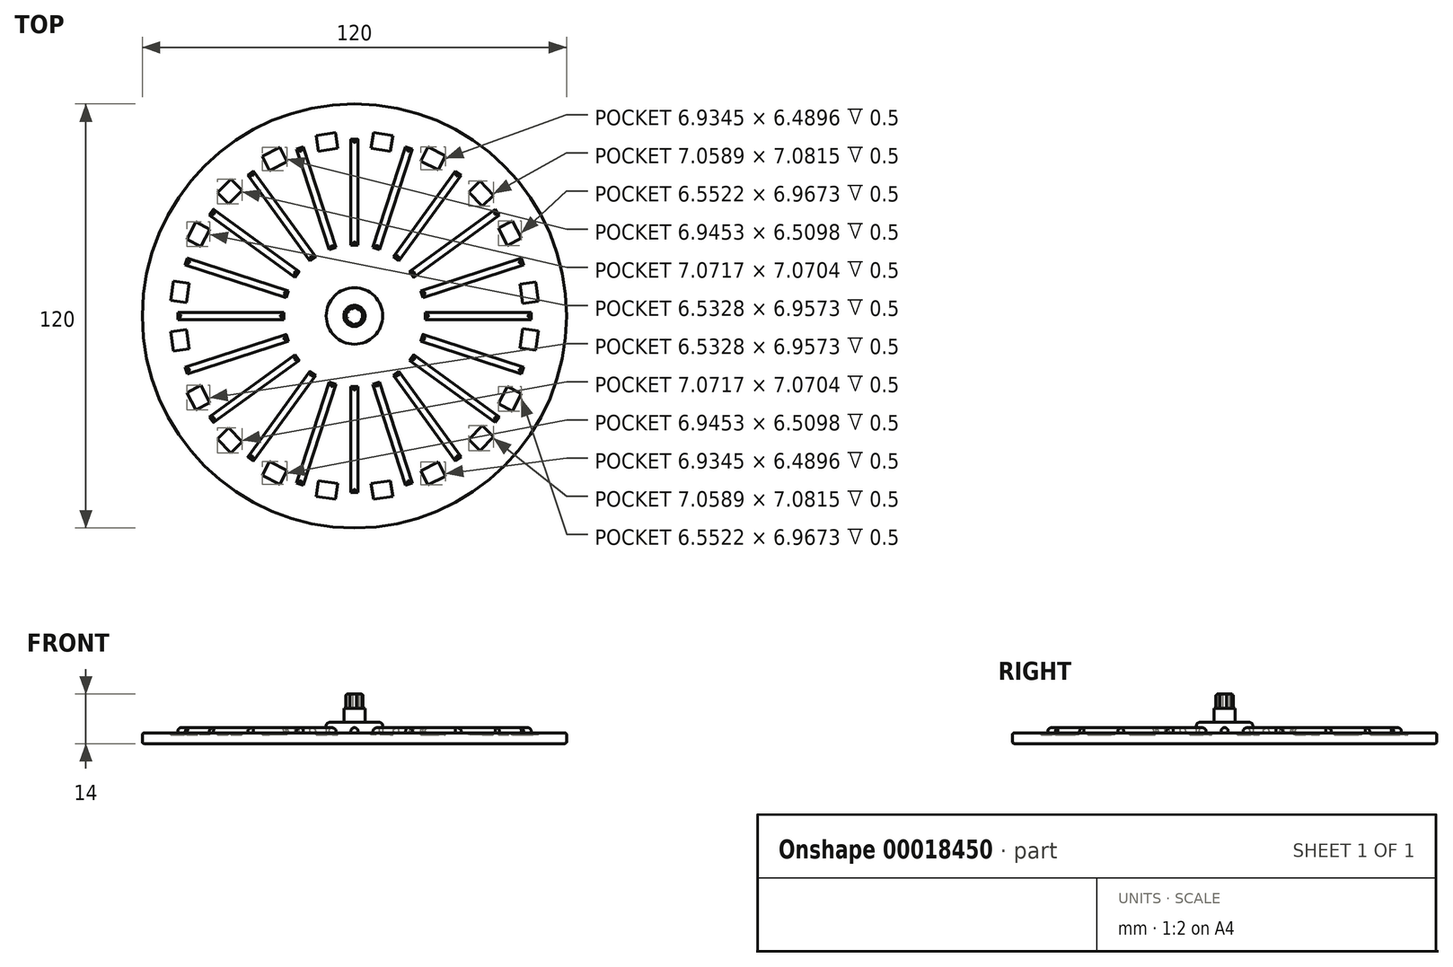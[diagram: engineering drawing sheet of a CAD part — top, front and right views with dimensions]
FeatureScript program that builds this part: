
annotation { "Feature Type Name" : "Feature", "Feature Type Description" : "" }
export const myFeature = defineFeature(function(context is Context, id is Id, definition is map)
    precondition{}
    {
        {
            var Q0;
            Q0=qCreatedBy(makeId("Top.planeOp"),FACE);
            var sketch = newSketch(context, id + "F0", { "sketchPlane" : qUnion([Q0])});
            skCircle(sketch, "E0", {"center": v(0, 0) * mm, "radius": 60 * mm});
            skSolve(sketch);
        }
        {
            var Q0;
            Q0=makeQuery(id+"F0.imprint","IMPRINT",FACE,{"disambiguationData":[TD([[makeQuery(id+"F0.imprint","IMPRINT",EDGE,{"derivedFrom":sQuery(id+"F0.wireOp",EDGE,"E0")}),1.0]])]});
            extrude(context, id + "F1", {"entities" : qUnion([Q0]), "depth" : 3 * mm});
        }
        {
            var Q0;
            Q0=makeQuery(id+"F1.opExtrude","CAP_EDGE",EDGE,{"disambiguationData":[OSD([sQuery(id+"F0.wireOp",EDGE,"E0")])],"isStart":false});
            var Q1;
            Q1=makeQuery(id+"F1.opExtrude","CAP_EDGE",EDGE,{"disambiguationData":[OSD([sQuery(id+"F0.wireOp",EDGE,"E0")])],"isStart":true});
            fillet(context, id + "F2", {"entities" : qUnion([Q0, Q1]), "radius" : 0.5 * mm, "tangentPropagation" : true, "allowEdgeOverflow" : false});
        }
        {
            var Q0;
            Q0=makeQuery(id+"F1.opExtrude","CAP_FACE",FACE,{"disambiguationData":[OSD([sQuery(id+"F0.wireOp",EDGE,"E0")])],"isStart":false});
            var sketch = newSketch(context, id + "F3", { "sketchPlane" : qUnion([Q0])});
            skLineSegment(sketch, "E1", {"start": v(0, 0) * mm, "end": v(0, 59.5) * mm, "construction": true});
            skCircle(sketch, "E2", {"center": v(0, 0) * mm, "radius": 20 * mm, "construction": true});
            skCircle(sketch, "E3", {"center": v(0, 0) * mm, "radius": 50 * mm, "construction": true});
            skCircle(sketch, "E4", {"center": v(0, 0) * mm, "radius": 35 * mm, "construction": true});
            skLineSegment(sketch, "E5.rect.bottom", {"start": v(1, 49.99) * mm, "end": v(-1, 49.99) * mm});
            skLineSegment(sketch, "E5.rect.top", {"start": v(1, 20.01) * mm, "end": v(-1, 20.01) * mm});
            skLineSegment(sketch, "E5.rect.left", {"start": v(1, 49.99) * mm, "end": v(1, 20.01) * mm});
            skLineSegment(sketch, "E5.rect.right", {"start": v(-1, 49.99) * mm, "end": v(-1, 20.01) * mm});
            skPoint(sketch, "E5.rect.middle", {"position": v(0, 35) * mm});
            skCircle(sketch, "E6", {"center": v(0, 0) * mm, "radius": 8 * mm});
            skCircle(sketch, "E7", {"center": v(0, 0) * mm, "radius": 45 * mm, "construction": true});
            skSolve(sketch);
        }
        {
            var Q0;
            Q0=makeQuery(id+"F3.imprint","IMPRINT",FACE,{"disambiguationData":[TD([[makeQuery(id+"F3.imprint","IMPRINT",EDGE,{"derivedFrom":sQuery(id+"F3.wireOp",EDGE,"E5.rect.bottom")}),1.0]])]});
            extrude(context, id + "F4", {"entities" : qUnion([Q0]), "depth" : 1.5 * mm});
        }
        {
            var Q0;
            Q0=makeQuery(id+"F4.opExtrude","CAP_EDGE",EDGE,{"disambiguationData":[OSD([sQuery(id+"F3.wireOp",EDGE,"E5.rect.left")])],"isStart":false});
            var Q1;
            Q1=makeQuery(id+"F4.opExtrude","CAP_EDGE",EDGE,{"disambiguationData":[OSD([sQuery(id+"F3.wireOp",EDGE,"E5.rect.right")])],"isStart":false});
            var Q2;
            Q2=makeQuery(id+"F4.opExtrude","CAP_EDGE",EDGE,{"disambiguationData":[OSD([sQuery(id+"F3.wireOp",EDGE,"E5.rect.top")])],"isStart":false});
            var Q3;
            Q3=makeQuery(id+"F4.opExtrude","CAP_EDGE",EDGE,{"disambiguationData":[OSD([sQuery(id+"F3.wireOp",EDGE,"E5.rect.bottom")])],"isStart":false});
            fillet(context, id + "F5", {"entities" : qUnion([Q0, Q1, Q2, Q3]), "radius" : 1 * mm, "tangentPropagation" : true, "allowEdgeOverflow" : false});
        }
        {
            var Q0;
            Q0=makeQuery(id+"F4.opExtrude","SWEPT_BODY",BODY,{"disambiguationData":[OSD([sQuery(id+"F3.wireOp",EDGE,"E5.rect.bottom"),sQuery(id+"F3.wireOp",EDGE,"E5.rect.top"),sQuery(id+"F3.wireOp",EDGE,"E5.rect.left"),sQuery(id+"F3.wireOp",EDGE,"E5.rect.right")])]});
            var Q1;
            {var subQ0=sQuery(id+"F0.wireOp",EDGE,"E0");Q1=makeQuery(id+"F2.opFillet","BLEND_EDGE",EDGE,{"blendedFrom":[makeQuery(id+"F1.opExtrude","CAP_EDGE",EDGE,{"disambiguationData":[OSD([subQ0])],"isStart":false}),makeQuery(id+"F1.opExtrude","SWEPT_FACE",FACE,{"disambiguationData":[OSD([subQ0])]})],"blendedInto":[makeQuery(id+"F1.opExtrude","SWEPT_FACE",FACE,{"disambiguationData":[OSD([subQ0])]})]});}
            circularPattern(context, id + "F6", {"operationType" : NewBodyOperationType.ADD, "entities" : qUnion([Q0]), "axis" : qUnion([Q1]), "angle" : 18 * degree, "instanceCount" : round(23)});
        }
        {
            var Q0;
            Q0=makeQuery(id+"F3.imprint","IMPRINT",FACE,{"disambiguationData":[TD([[makeQuery(id+"F3.imprint","IMPRINT",EDGE,{"derivedFrom":sQuery(id+"F3.wireOp",EDGE,"E6")}),1.0]])]});
            extrude(context, id + "F7", {"entities" : qUnion([Q0]), "operationType" : NewBodyOperationType.ADD, "depth" : 3 * mm});
        }
        {
            var Q0;
            Q0=makeQuery(id+"F7.opExtrude","CAP_EDGE",EDGE,{"disambiguationData":[OSD([sQuery(id+"F3.wireOp",EDGE,"E6")])],"isStart":false});
            fillet(context, id + "F8", {"entities" : qUnion([Q0]), "radius" : 1 * mm, "tangentPropagation" : true, "allowEdgeOverflow" : false});
        }
        {
            var Q0;
            Q0=makeQuery(id+"F7.opExtrude","CAP_FACE",FACE,{"disambiguationData":[OSD([sQuery(id+"F3.wireOp",EDGE,"E6")])],"isStart":false});
            var sketch = newSketch(context, id + "F9", { "sketchPlane" : qUnion([Q0])});
            skCircle(sketch, "E8", {"center": v(0, 0) * mm, "radius": 3 * mm});
            skSolve(sketch);
        }
        {
            var Q0;
            Q0=makeQuery(id+"F9.imprint","IMPRINT",FACE,{"disambiguationData":[TD([[makeQuery(id+"F9.imprint","IMPRINT",EDGE,{"derivedFrom":sQuery(id+"F9.wireOp",EDGE,"E8")}),1.0]])]});
            extrude(context, id + "F10", {"entities" : qUnion([Q0]), "operationType" : NewBodyOperationType.ADD, "depth" : 4 * mm});
        }
        {
            var Q0;
            Q0=makeQuery(id+"F10.opExtrude","CAP_FACE",FACE,{"disambiguationData":[OSD([sQuery(id+"F9.wireOp",EDGE,"E8")])],"isStart":false});
            var sketch = newSketch(context, id + "F11", { "sketchPlane" : qUnion([Q0])});
            skCircle(sketch, "E9.cCircle", {"center": v(0, 0) * mm, "radius": 2.5 * mm, "construction": true});
            skLineSegment(sketch, "E9.0", {"start": v(2.13, -1.3) * mm, "end": v(0.59, -2.43) * mm});
            skLineSegment(sketch, "E9.1", {"start": v(0.59, -2.43) * mm, "end": v(-1.3, -2.13) * mm});
            skLineSegment(sketch, "E9.2", {"start": v(-1.3, -2.13) * mm, "end": v(-2.43, -0.59) * mm});
            skLineSegment(sketch, "E9.3", {"start": v(-2.43, -0.59) * mm, "end": v(-2.13, 1.3) * mm});
            skLineSegment(sketch, "E9.4", {"start": v(-2.13, 1.3) * mm, "end": v(-0.59, 2.43) * mm});
            skLineSegment(sketch, "E9.5", {"start": v(-0.59, 2.43) * mm, "end": v(1.3, 2.13) * mm});
            skLineSegment(sketch, "E9.6", {"start": v(1.3, 2.13) * mm, "end": v(2.43, 0.59) * mm});
            skLineSegment(sketch, "E9.7", {"start": v(2.43, 0.59) * mm, "end": v(2.13, -1.3) * mm});
            skSolve(sketch);
        }
        {
            var Q0;
            Q0=makeQuery(id+"F11.imprint","IMPRINT",FACE,{"disambiguationData":[TD([[makeQuery(id+"F11.imprint","IMPRINT",EDGE,{"derivedFrom":sQuery(id+"F11.wireOp",EDGE,"E9.0")}),-1.0]])]});
            extrude(context, id + "F12", {"entities" : qUnion([Q0]), "operationType" : NewBodyOperationType.ADD, "depth" : 4 * mm});
        }
        {
            var Q0;
            Q0=makeQuery(id+"F12.opExtrude","CAP_EDGE",EDGE,{"disambiguationData":[OSD([sQuery(id+"F11.wireOp",EDGE,"E9.3")])],"isStart":false});
            var Q1;
            Q1=makeQuery(id+"F12.opExtrude","CAP_EDGE",EDGE,{"disambiguationData":[OSD([sQuery(id+"F11.wireOp",EDGE,"E9.2")])],"isStart":false});
            var Q2;
            Q2=makeQuery(id+"F12.opExtrude","CAP_EDGE",EDGE,{"disambiguationData":[OSD([sQuery(id+"F11.wireOp",EDGE,"E9.1")])],"isStart":false});
            var Q3;
            Q3=makeQuery(id+"F12.opExtrude","CAP_EDGE",EDGE,{"disambiguationData":[OSD([sQuery(id+"F11.wireOp",EDGE,"E9.4")])],"isStart":false});
            var Q4;
            Q4=makeQuery(id+"F12.opExtrude","CAP_EDGE",EDGE,{"disambiguationData":[OSD([sQuery(id+"F11.wireOp",EDGE,"E9.5")])],"isStart":false});
            var Q5;
            Q5=makeQuery(id+"F12.opExtrude","CAP_EDGE",EDGE,{"disambiguationData":[OSD([sQuery(id+"F11.wireOp",EDGE,"E9.6")])],"isStart":false});
            var Q6;
            Q6=makeQuery(id+"F12.opExtrude","CAP_EDGE",EDGE,{"disambiguationData":[OSD([sQuery(id+"F11.wireOp",EDGE,"E9.7")])],"isStart":false});
            var Q7;
            Q7=makeQuery(id+"F12.opExtrude","CAP_EDGE",EDGE,{"disambiguationData":[OSD([sQuery(id+"F11.wireOp",EDGE,"E9.0")])],"isStart":false});
            fillet(context, id + "F13", {"entities" : qUnion([Q0, Q1, Q2, Q3, Q4, Q5, Q6, Q7]), "radius" : 0.5 * mm, "allowEdgeOverflow" : false});
        }
        {
            var Q0;
            Q0=makeQuery(id+"F3.imprint","IMPRINT",FACE,{"disambiguationData":[TD([[makeQuery(id+"F3.imprint","IMPRINT",EDGE,{"derivedFrom":sQuery(id+"F3.wireOp",EDGE,"E5.rect.bottom")}),-1.0]])]});
            var sketch = newSketch(context, id + "F14", { "sketchPlane" : qUnion([Q0])});
            skLineSegment(sketch, "E10", {"start": v(0, 0) * mm, "end": v(9.16, 58.76) * mm, "construction": true});
            skLineSegment(sketch, "E11", {"start": v(0, 0) * mm, "end": v(18.06, 56.37) * mm, "construction": true});
            skLineSegment(sketch, "E12", {"start": v(0, 0) * mm, "end": v(0, 59.7) * mm, "construction": true});
            skLineSegment(sketch, "E13", {"start": v(0, 59.7) * mm, "end": v(9.16, 58.76) * mm, "construction": true});
            skLineSegment(sketch, "E14", {"start": v(9.16, 58.76) * mm, "end": v(0, 59.7) * mm, "construction": true});
            skLineSegment(sketch, "E15", {"start": v(9.16, 58.76) * mm, "end": v(18.06, 56.37) * mm, "construction": true});
            skLineSegment(sketch, "E16", {"start": v(7.33, 47.02) * mm, "end": v(4.7, 47.43) * mm});
            skLineSegment(sketch, "E17", {"start": v(7.33, 47.02) * mm, "end": v(10.14, 46.58) * mm});
            skLineSegment(sketch, "E18", {"start": v(10.14, 46.58) * mm, "end": v(10.83, 51.03) * mm});
            skLineSegment(sketch, "E19", {"start": v(10.83, 51.03) * mm, "end": v(5.4, 51.87) * mm});
            skLineSegment(sketch, "E20", {"start": v(5.4, 51.87) * mm, "end": v(4.7, 47.43) * mm});
            skLineSegment(sketch, "E21.0.MirrorCS", {"start": v(-10.83, 51.03) * mm, "end": v(-5.4, 51.87) * mm});
            skLineSegment(sketch, "E22.0.MirrorCS", {"start": v(-5.4, 51.87) * mm, "end": v(-4.7, 47.43) * mm});
            skLineSegment(sketch, "E23.0.MirrorCS", {"start": v(-10.14, 46.58) * mm, "end": v(-10.83, 51.03) * mm});
            skLineSegment(sketch, "E24.0.MirrorCS", {"start": v(-7.33, 47.02) * mm, "end": v(-4.7, 47.43) * mm});
            skLineSegment(sketch, "E25.0.MirrorCS", {"start": v(-7.33, 47.02) * mm, "end": v(-10.14, 46.58) * mm});
            skLineSegment(sketch, "E26.0.MirrorCS", {"start": v(21.36, 42.52) * mm, "end": v(18.81, 43.8) * mm});
            skLineSegment(sketch, "E27.0.MirrorCS", {"start": v(25.75, 45.35) * mm, "end": v(23.73, 41.33) * mm});
            skLineSegment(sketch, "E28.0.MirrorCS", {"start": v(18.81, 43.8) * mm, "end": v(20.83, 47.82) * mm});
            skLineSegment(sketch, "E29.0.MirrorCS", {"start": v(20.83, 47.82) * mm, "end": v(25.75, 45.35) * mm});
            skLineSegment(sketch, "E30.0.MirrorCS", {"start": v(21.36, 42.52) * mm, "end": v(23.73, 41.33) * mm});
            skLineSegment(sketch, "E31", {"start": v(0, 0) * mm, "end": v(-18.56, 57.25) * mm, "construction": true});
            skLineSegment(sketch, "E32", {"start": v(0, 0) * mm, "end": v(-34.89, 48) * mm, "construction": true});
            skLineSegment(sketch, "E33.0.MirrorCS", {"start": v(-19.12, 43.67) * mm, "end": v(-21.17, 47.68) * mm});
            skLineSegment(sketch, "E34.0.MirrorCS", {"start": v(-26.07, 45.17) * mm, "end": v(-24.02, 41.17) * mm});
            skLineSegment(sketch, "E35.0.MirrorCS", {"start": v(-21.17, 47.68) * mm, "end": v(-26.07, 45.17) * mm});
            skLineSegment(sketch, "E36.0.MirrorCS", {"start": v(-21.65, 42.37) * mm, "end": v(-19.12, 43.67) * mm});
            skLineSegment(sketch, "E37.0.MirrorCS", {"start": v(-21.65, 42.37) * mm, "end": v(-24.02, 41.17) * mm});
            skLineSegment(sketch, "E38.0.MirrorCS", {"start": v(-33.62, 33.68) * mm, "end": v(-31.74, 35.55) * mm});
            skLineSegment(sketch, "E39.0.MirrorCS", {"start": v(-33.62, 33.68) * mm, "end": v(-35.63, 31.67) * mm});
            skLineSegment(sketch, "E40.0.MirrorCS", {"start": v(-35.63, 31.67) * mm, "end": v(-38.81, 34.85) * mm});
            skLineSegment(sketch, "E41.0.MirrorCS", {"start": v(-38.81, 34.85) * mm, "end": v(-34.92, 38.74) * mm});
            skLineSegment(sketch, "E42.0.MirrorCS", {"start": v(-34.92, 38.74) * mm, "end": v(-31.74, 35.55) * mm});
            skLineSegment(sketch, "E43", {"start": v(0, 0) * mm, "end": v(-48.36, 35.52) * mm, "construction": true});
            skLineSegment(sketch, "E44", {"start": v(0, 0) * mm, "end": v(-58.04, 18.6) * mm, "construction": true});
            skLineSegment(sketch, "E45", {"start": v(0, 0) * mm, "end": v(61.65, 0) * mm, "construction": true});
            skLineSegment(sketch, "E46", {"start": v(61.65, 0) * mm, "end": v(-61.86, 0) * mm, "construction": true});
            skLineSegment(sketch, "E47", {"start": v(0, 0) * mm, "end": v(34.29, 46.69) * mm, "construction": true});
            skLineSegment(sketch, "E48", {"start": v(0, 0) * mm, "end": v(48.15, 35) * mm, "construction": true});
            skLineSegment(sketch, "E49", {"start": v(0, 0) * mm, "end": v(57.22, 18.4) * mm, "construction": true});
            skLineSegment(sketch, "E50.0.MirrorCS", {"start": v(-40.88, 24.52) * mm, "end": v(-44.87, 26.6) * mm});
            skLineSegment(sketch, "E51.0.MirrorCS", {"start": v(-47.41, 21.72) * mm, "end": v(-43.42, 19.64) * mm});
            skLineSegment(sketch, "E52.0.MirrorCS", {"start": v(-44.87, 26.6) * mm, "end": v(-47.41, 21.72) * mm});
            skLineSegment(sketch, "E53.0.MirrorCS", {"start": v(-42.2, 22) * mm, "end": v(-40.88, 24.52) * mm});
            skLineSegment(sketch, "E54.0.MirrorCS", {"start": v(-42.2, 22) * mm, "end": v(-43.42, 19.64) * mm});
            skLineSegment(sketch, "E55.0.MirrorCS", {"start": v(-51.2, 9.88) * mm, "end": v(-46.75, 9.25) * mm});
            skLineSegment(sketch, "E56.0.MirrorCS", {"start": v(-47.52, 3.8) * mm, "end": v(-51.97, 4.43) * mm});
            skLineSegment(sketch, "E57.0.MirrorCS", {"start": v(-51.97, 4.43) * mm, "end": v(-51.2, 9.88) * mm});
            skLineSegment(sketch, "E58.0.MirrorCS", {"start": v(-47.12, 6.62) * mm, "end": v(-47.52, 3.8) * mm});
            skLineSegment(sketch, "E59.0.MirrorCS", {"start": v(-47.12, 6.62) * mm, "end": v(-46.75, 9.25) * mm});
            skLineSegment(sketch, "E60.0.MirrorCS", {"start": v(39.4, 34.2) * mm, "end": v(35.57, 38.14) * mm});
            skLineSegment(sketch, "E61.0.MirrorCS", {"start": v(36.16, 31.06) * mm, "end": v(39.4, 34.2) * mm});
            skLineSegment(sketch, "E62.0.MirrorCS", {"start": v(35.57, 38.14) * mm, "end": v(32.33, 35.01) * mm});
            skLineSegment(sketch, "E63.0.MirrorCS", {"start": v(34.18, 33.1) * mm, "end": v(32.33, 35.01) * mm});
            skLineSegment(sketch, "E64.0.MirrorCS", {"start": v(34.18, 33.1) * mm, "end": v(36.16, 31.06) * mm});
            skLineSegment(sketch, "E65.0.MirrorCS", {"start": v(42.04, 22.3) * mm, "end": v(40.7, 24.8) * mm});
            skLineSegment(sketch, "E66.0.MirrorCS", {"start": v(47.26, 22.05) * mm, "end": v(43.29, 19.95) * mm});
            skLineSegment(sketch, "E67.0.MirrorCS", {"start": v(44.68, 26.91) * mm, "end": v(47.26, 22.05) * mm});
            skLineSegment(sketch, "E68.0.MirrorCS", {"start": v(40.7, 24.8) * mm, "end": v(44.68, 26.91) * mm});
            skLineSegment(sketch, "E69.0.MirrorCS", {"start": v(42.04, 22.3) * mm, "end": v(43.29, 19.95) * mm});
            skLineSegment(sketch, "E70.0.MirrorCS", {"start": v(47.15, 6.4) * mm, "end": v(46.8, 9.02) * mm});
            skLineSegment(sketch, "E71.0.MirrorCS", {"start": v(51.26, 9.63) * mm, "end": v(46.8, 9.02) * mm});
            skLineSegment(sketch, "E72.0.MirrorCS", {"start": v(52, 4.18) * mm, "end": v(51.26, 9.63) * mm});
            skLineSegment(sketch, "E73.0.MirrorCS", {"start": v(47.54, 3.57) * mm, "end": v(52, 4.18) * mm});
            skLineSegment(sketch, "E74.0.MirrorCS", {"start": v(47.15, 6.4) * mm, "end": v(47.54, 3.57) * mm});
            skLineSegment(sketch, "E75.0.MirrorCS", {"start": v(-47.52, -3.8) * mm, "end": v(-51.97, -4.43) * mm});
            skLineSegment(sketch, "E76.0.MirrorCS", {"start": v(-51.97, -4.43) * mm, "end": v(-51.2, -9.88) * mm});
            skLineSegment(sketch, "E77.0.MirrorCS", {"start": v(-47.12, -6.62) * mm, "end": v(-46.75, -9.25) * mm});
            skLineSegment(sketch, "E78.0.MirrorCS", {"start": v(-47.12, -6.62) * mm, "end": v(-47.52, -3.8) * mm});
            skLineSegment(sketch, "E79.0.MirrorCS", {"start": v(-51.2, -9.88) * mm, "end": v(-46.75, -9.25) * mm});
            skLineSegment(sketch, "E80.0.MirrorCS", {"start": v(-47.41, -21.72) * mm, "end": v(-43.42, -19.64) * mm});
            skLineSegment(sketch, "E81.0.MirrorCS", {"start": v(-44.87, -26.6) * mm, "end": v(-47.41, -21.72) * mm});
            skLineSegment(sketch, "E82.0.MirrorCS", {"start": v(-42.2, -22) * mm, "end": v(-43.42, -19.64) * mm});
            skLineSegment(sketch, "E83.0.MirrorCS", {"start": v(-42.2, -22) * mm, "end": v(-40.88, -24.52) * mm});
            skLineSegment(sketch, "E84.0.MirrorCS", {"start": v(-40.88, -24.52) * mm, "end": v(-44.87, -26.6) * mm});
            skLineSegment(sketch, "E85.0.MirrorCS", {"start": v(-35.63, -31.67) * mm, "end": v(-38.81, -34.85) * mm});
            skLineSegment(sketch, "E86.0.MirrorCS", {"start": v(-38.81, -34.85) * mm, "end": v(-34.92, -38.74) * mm});
            skLineSegment(sketch, "E87.0.MirrorCS", {"start": v(-34.92, -38.74) * mm, "end": v(-31.74, -35.55) * mm});
            skLineSegment(sketch, "E88.0.MirrorCS", {"start": v(-33.62, -33.68) * mm, "end": v(-31.74, -35.55) * mm});
            skLineSegment(sketch, "E89.0.MirrorCS", {"start": v(-33.62, -33.68) * mm, "end": v(-35.63, -31.67) * mm});
            skLineSegment(sketch, "E90.0.MirrorCS", {"start": v(-21.65, -42.37) * mm, "end": v(-24.02, -41.17) * mm});
            skLineSegment(sketch, "E91.0.MirrorCS", {"start": v(-21.65, -42.37) * mm, "end": v(-19.12, -43.67) * mm});
            skLineSegment(sketch, "E92.0.MirrorCS", {"start": v(-19.12, -43.67) * mm, "end": v(-21.17, -47.68) * mm});
            skLineSegment(sketch, "E93.0.MirrorCS", {"start": v(-21.17, -47.68) * mm, "end": v(-26.07, -45.17) * mm});
            skLineSegment(sketch, "E94.0.MirrorCS", {"start": v(-26.07, -45.17) * mm, "end": v(-24.02, -41.17) * mm});
            skLineSegment(sketch, "E95.0.MirrorCS", {"start": v(-7.33, -47.02) * mm, "end": v(-10.14, -46.58) * mm});
            skLineSegment(sketch, "E96.0.MirrorCS", {"start": v(-7.33, -47.02) * mm, "end": v(-4.7, -47.43) * mm});
            skLineSegment(sketch, "E97.0.MirrorCS", {"start": v(-5.4, -51.87) * mm, "end": v(-4.7, -47.43) * mm});
            skLineSegment(sketch, "E98.0.MirrorCS", {"start": v(-10.14, -46.58) * mm, "end": v(-10.83, -51.03) * mm});
            skLineSegment(sketch, "E99.0.MirrorCS", {"start": v(-10.83, -51.03) * mm, "end": v(-5.4, -51.87) * mm});
            skLineSegment(sketch, "E100.0.MirrorCS", {"start": v(5.4, -51.87) * mm, "end": v(4.7, -47.43) * mm});
            skLineSegment(sketch, "E101.0.MirrorCS", {"start": v(7.33, -47.02) * mm, "end": v(4.7, -47.43) * mm});
            skLineSegment(sketch, "E102.0.MirrorCS", {"start": v(7.33, -47.02) * mm, "end": v(10.14, -46.58) * mm});
            skLineSegment(sketch, "E103.0.MirrorCS", {"start": v(10.14, -46.58) * mm, "end": v(10.83, -51.03) * mm});
            skLineSegment(sketch, "E104.0.MirrorCS", {"start": v(10.83, -51.03) * mm, "end": v(5.4, -51.87) * mm});
            skLineSegment(sketch, "E105.0.MirrorCS", {"start": v(18.81, -43.8) * mm, "end": v(20.83, -47.82) * mm});
            skLineSegment(sketch, "E106.0.MirrorCS", {"start": v(20.83, -47.82) * mm, "end": v(25.75, -45.35) * mm});
            skLineSegment(sketch, "E107.0.MirrorCS", {"start": v(25.75, -45.35) * mm, "end": v(23.73, -41.33) * mm});
            skLineSegment(sketch, "E108.0.MirrorCS", {"start": v(21.36, -42.52) * mm, "end": v(18.81, -43.8) * mm});
            skLineSegment(sketch, "E109.0.MirrorCS", {"start": v(21.36, -42.52) * mm, "end": v(23.73, -41.33) * mm});
            skLineSegment(sketch, "E110.0.MirrorCS", {"start": v(35.57, -38.14) * mm, "end": v(32.33, -35.01) * mm});
            skLineSegment(sketch, "E111.0.MirrorCS", {"start": v(39.4, -34.2) * mm, "end": v(35.57, -38.14) * mm});
            skLineSegment(sketch, "E112.0.MirrorCS", {"start": v(36.16, -31.06) * mm, "end": v(39.4, -34.2) * mm});
            skLineSegment(sketch, "E113.0.MirrorCS", {"start": v(34.18, -33.1) * mm, "end": v(32.33, -35.01) * mm});
            skLineSegment(sketch, "E114.0.MirrorCS", {"start": v(34.18, -33.1) * mm, "end": v(36.16, -31.06) * mm});
            skLineSegment(sketch, "E115.0.MirrorCS", {"start": v(44.68, -26.91) * mm, "end": v(47.26, -22.05) * mm});
            skLineSegment(sketch, "E116.0.MirrorCS", {"start": v(40.7, -24.8) * mm, "end": v(44.68, -26.91) * mm});
            skLineSegment(sketch, "E117.0.MirrorCS", {"start": v(42.04, -22.3) * mm, "end": v(40.7, -24.8) * mm});
            skLineSegment(sketch, "E118.0.MirrorCS", {"start": v(42.04, -22.3) * mm, "end": v(43.29, -19.95) * mm});
            skLineSegment(sketch, "E119.0.MirrorCS", {"start": v(47.26, -22.05) * mm, "end": v(43.29, -19.95) * mm});
            skLineSegment(sketch, "E120.0.MirrorCS", {"start": v(51.26, -9.63) * mm, "end": v(46.8, -9.02) * mm});
            skLineSegment(sketch, "E121.0.MirrorCS", {"start": v(47.15, -6.4) * mm, "end": v(47.54, -3.57) * mm});
            skLineSegment(sketch, "E122.0.MirrorCS", {"start": v(47.15, -6.4) * mm, "end": v(46.8, -9.02) * mm});
            skLineSegment(sketch, "E123.0.MirrorCS", {"start": v(47.54, -3.57) * mm, "end": v(52, -4.18) * mm});
            skLineSegment(sketch, "E124.0.MirrorCS", {"start": v(52, -4.18) * mm, "end": v(51.26, -9.63) * mm});
            skSolve(sketch);
        }
        {
            var Q0;
            Q0=makeQuery(id+"F14.imprint","IMPRINT",FACE,{"disambiguationData":[TD([[makeQuery(id+"F14.imprint","IMPRINT",EDGE,{"derivedFrom":sQuery(id+"F14.wireOp",EDGE,"E16")}),-1.0]])]});
            var Q1;
            Q1=makeQuery(id+"F14.imprint","IMPRINT",FACE,{"disambiguationData":[TD([[makeQuery(id+"F14.imprint","IMPRINT",EDGE,{"derivedFrom":sQuery(id+"F14.wireOp",EDGE,"E21.0.MirrorCS")}),-1.0]])]});
            var Q2;
            Q2=makeQuery(id+"F14.imprint","IMPRINT",FACE,{"disambiguationData":[TD([[makeQuery(id+"F14.imprint","IMPRINT",EDGE,{"derivedFrom":sQuery(id+"F14.wireOp",EDGE,"E33.0.MirrorCS")}),1.0]])]});
            var Q3;
            Q3=makeQuery(id+"F14.imprint","IMPRINT",FACE,{"disambiguationData":[TD([[makeQuery(id+"F14.imprint","IMPRINT",EDGE,{"derivedFrom":sQuery(id+"F14.wireOp",EDGE,"E38.0.MirrorCS")}),1.0]])]});
            var Q4;
            Q4=makeQuery(id+"F14.imprint","IMPRINT",FACE,{"disambiguationData":[TD([[makeQuery(id+"F14.imprint","IMPRINT",EDGE,{"derivedFrom":sQuery(id+"F14.wireOp",EDGE,"E50.0.MirrorCS")}),1.0]])]});
            var Q5;
            Q5=makeQuery(id+"F14.imprint","IMPRINT",FACE,{"disambiguationData":[TD([[makeQuery(id+"F14.imprint","IMPRINT",EDGE,{"derivedFrom":sQuery(id+"F14.wireOp",EDGE,"E55.0.MirrorCS")}),-1.0]])]});
            var Q6;
            Q6=makeQuery(id+"F14.imprint","IMPRINT",FACE,{"disambiguationData":[TD([[makeQuery(id+"F14.imprint","IMPRINT",EDGE,{"derivedFrom":sQuery(id+"F14.wireOp",EDGE,"E75.0.MirrorCS")}),1.0]])]});
            var Q7;
            Q7=makeQuery(id+"F14.imprint","IMPRINT",FACE,{"disambiguationData":[TD([[makeQuery(id+"F14.imprint","IMPRINT",EDGE,{"derivedFrom":sQuery(id+"F14.wireOp",EDGE,"E80.0.MirrorCS")}),-1.0]])]});
            var Q8;
            Q8=makeQuery(id+"F14.imprint","IMPRINT",FACE,{"disambiguationData":[TD([[makeQuery(id+"F14.imprint","IMPRINT",EDGE,{"derivedFrom":sQuery(id+"F14.wireOp",EDGE,"E85.0.MirrorCS")}),1.0]])]});
            var Q9;
            Q9=makeQuery(id+"F14.imprint","IMPRINT",FACE,{"disambiguationData":[TD([[makeQuery(id+"F14.imprint","IMPRINT",EDGE,{"derivedFrom":sQuery(id+"F14.wireOp",EDGE,"E90.0.MirrorCS")}),1.0]])]});
            var Q10;
            Q10=makeQuery(id+"F14.imprint","IMPRINT",FACE,{"disambiguationData":[TD([[makeQuery(id+"F14.imprint","IMPRINT",EDGE,{"derivedFrom":sQuery(id+"F14.wireOp",EDGE,"E95.0.MirrorCS")}),1.0]])]});
            var Q11;
            Q11=makeQuery(id+"F14.imprint","IMPRINT",FACE,{"disambiguationData":[TD([[makeQuery(id+"F14.imprint","IMPRINT",EDGE,{"derivedFrom":sQuery(id+"F14.wireOp",EDGE,"E100.0.MirrorCS")}),-1.0]])]});
            var Q12;
            Q12=makeQuery(id+"F14.imprint","IMPRINT",FACE,{"disambiguationData":[TD([[makeQuery(id+"F14.imprint","IMPRINT",EDGE,{"derivedFrom":sQuery(id+"F14.wireOp",EDGE,"E105.0.MirrorCS")}),1.0]])]});
            var Q13;
            Q13=makeQuery(id+"F14.imprint","IMPRINT",FACE,{"disambiguationData":[TD([[makeQuery(id+"F14.imprint","IMPRINT",EDGE,{"derivedFrom":sQuery(id+"F14.wireOp",EDGE,"E110.0.MirrorCS")}),-1.0]])]});
            var Q14;
            Q14=makeQuery(id+"F14.imprint","IMPRINT",FACE,{"disambiguationData":[TD([[makeQuery(id+"F14.imprint","IMPRINT",EDGE,{"derivedFrom":sQuery(id+"F14.wireOp",EDGE,"E115.0.MirrorCS")}),1.0]])]});
            var Q15;
            Q15=makeQuery(id+"F14.imprint","IMPRINT",FACE,{"disambiguationData":[TD([[makeQuery(id+"F14.imprint","IMPRINT",EDGE,{"derivedFrom":sQuery(id+"F14.wireOp",EDGE,"E121.0.MirrorCS")}),-1.0]])]});
            var Q16;
            Q16=makeQuery(id+"F14.imprint","IMPRINT",FACE,{"disambiguationData":[TD([[makeQuery(id+"F14.imprint","IMPRINT",EDGE,{"derivedFrom":sQuery(id+"F14.wireOp",EDGE,"E70.0.MirrorCS")}),-1.0]])]});
            var Q17;
            Q17=makeQuery(id+"F14.imprint","IMPRINT",FACE,{"disambiguationData":[TD([[makeQuery(id+"F14.imprint","IMPRINT",EDGE,{"derivedFrom":sQuery(id+"F14.wireOp",EDGE,"E65.0.MirrorCS")}),-1.0]])]});
            var Q18;
            Q18=makeQuery(id+"F14.imprint","IMPRINT",FACE,{"disambiguationData":[TD([[makeQuery(id+"F14.imprint","IMPRINT",EDGE,{"derivedFrom":sQuery(id+"F14.wireOp",EDGE,"E60.0.MirrorCS")}),1.0]])]});
            var Q19;
            Q19=makeQuery(id+"F14.imprint","IMPRINT",FACE,{"disambiguationData":[TD([[makeQuery(id+"F14.imprint","IMPRINT",EDGE,{"derivedFrom":sQuery(id+"F14.wireOp",EDGE,"E26.0.MirrorCS")}),-1.0]])]});
            extrude(context, id + "F15", {"entities" : qUnion([Q0, Q1, Q2, Q3, Q4, Q5, Q6, Q7, Q8, Q9, Q10, Q11, Q12, Q13, Q14, Q15, Q16, Q17, Q18, Q19]), "operationType" : NewBodyOperationType.REMOVE, "oppositeDirection" : true, "depth" : 0.5 * mm});
        }
    });
